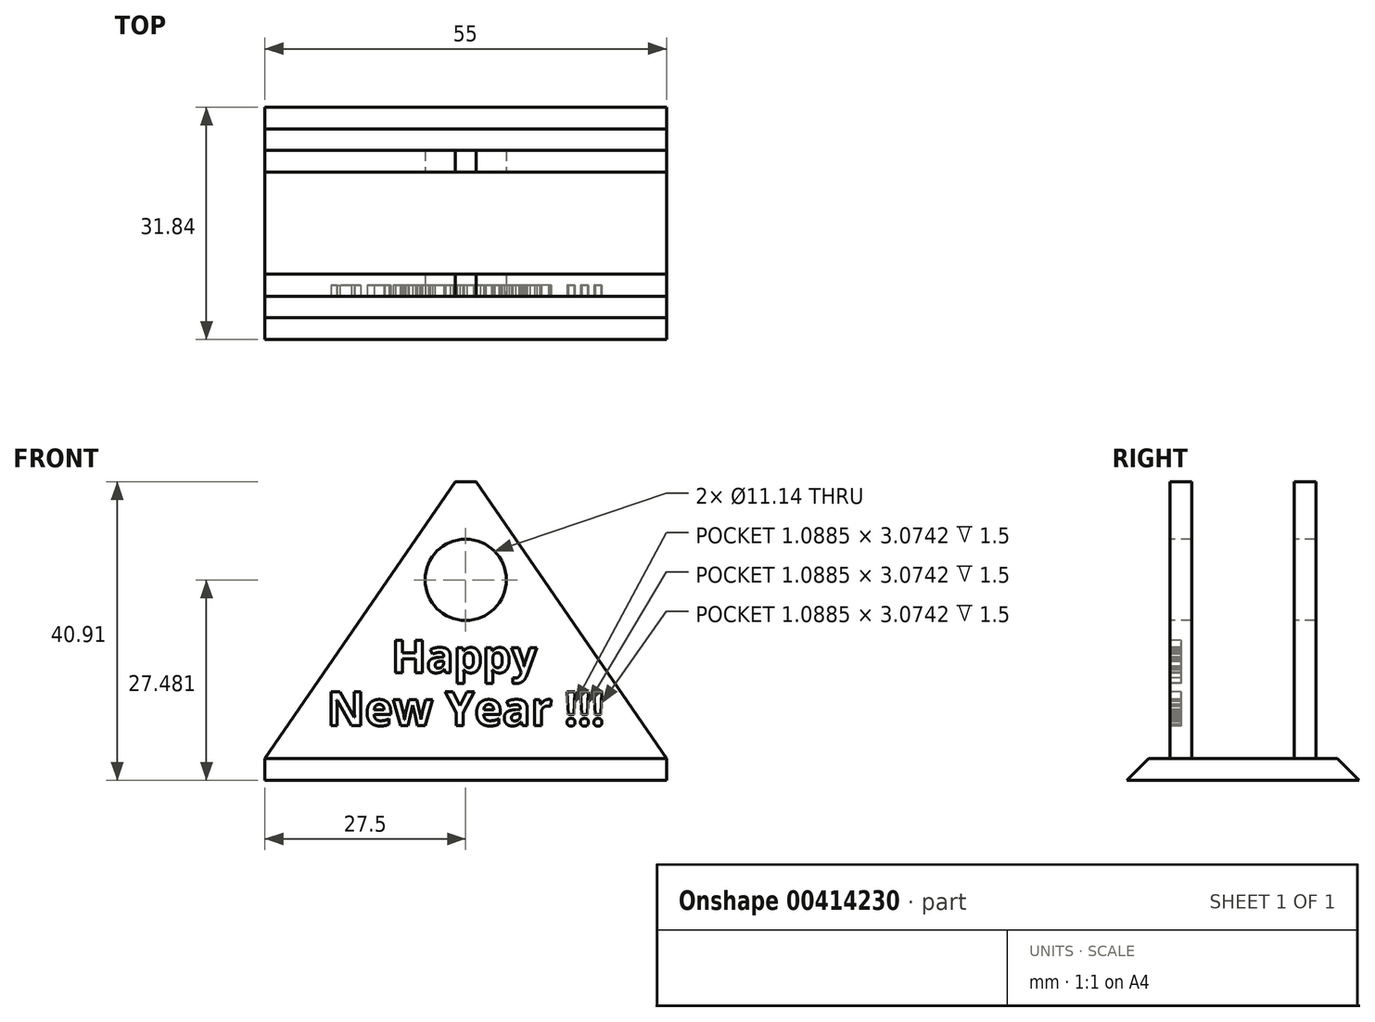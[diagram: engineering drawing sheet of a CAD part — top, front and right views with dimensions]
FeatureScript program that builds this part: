
annotation { "Feature Type Name" : "Feature", "Feature Type Description" : "" }
export const myFeature = defineFeature(function(context is Context, id is Id, definition is map)
    precondition{}
    {
        {
            var Q0;
            Q0=qCreatedBy(makeId("Top.planeOp"),FACE);
            var sketch = newSketch(context, id + "F0", { "sketchPlane" : qUnion([Q0])});
            skLineSegment(sketch, "E0.bottom", {"start": v(27.5, -7) * mm, "end": v(-27.5, -7) * mm});
            skLineSegment(sketch, "E0.top", {"start": v(27.5, 7) * mm, "end": v(-27.5, 7) * mm});
            skLineSegment(sketch, "E0.left", {"start": v(27.5, -7) * mm, "end": v(27.5, 7) * mm});
            skLineSegment(sketch, "E0.right", {"start": v(-27.5, -7) * mm, "end": v(-27.5, 7) * mm});
            skPoint(sketch, "E0.middle", {"position": v(0, 0) * mm});
            skSolve(sketch);
        }
        {
            var Q0;
            Q0=makeQuery(id+"F0.imprint","IMPRINT",FACE,{"disambiguationData":[TD([[makeQuery(id+"F0.imprint","IMPRINT",EDGE,{"derivedFrom":sQuery(id+"F0.wireOp",EDGE,"E0.bottom")}),-1.0]])]});
            extrude(context, id + "F1", {"entities" : qUnion([Q0]), "depth" : 3 * mm});
        }
        {
            var Q0;
            Q0=makeQuery(id+"F1.opExtrude","SWEPT_FACE",FACE,{"disambiguationData":[OSD([sQuery(id+"F0.wireOp",EDGE,"E0.bottom")])]});
            var sketch = newSketch(context, id + "F2", { "sketchPlane" : qUnion([Q0])});
            skLineSegment(sketch, "E1", {"start": v(0, 3) * mm, "end": v(0, 43) * mm, "construction": true});
            skPoint(sketch, "E1.endSnap0", {"position": v(0, 3) * mm});
            skLineSegment(sketch, "E2", {"start": v(0, 43) * mm, "end": v(-27.5, 3) * mm});
            skLineSegment(sketch, "E3", {"start": v(-27.5, 3) * mm, "end": v(-27.5, 0) * mm});
            skLineSegment(sketch, "E4", {"start": v(-27.5, 0) * mm, "end": v(27.5, 0) * mm});
            skLineSegment(sketch, "E5", {"start": v(27.5, 0) * mm, "end": v(27.5, 3) * mm});
            skLineSegment(sketch, "E6", {"start": v(27.5, 3) * mm, "end": v(0, 43) * mm});
            skSolve(sketch);
        }
        {
            var Q0;
            Q0=makeQuery(id+"F2.imprint","IMPRINT",FACE,{"disambiguationData":[TD([[makeQuery(id+"F2.imprint","IMPRINT",EDGE,{"derivedFrom":sQuery(id+"F2.wireOp",EDGE,"E3")}),1.0]])]});
            var Q1;
            Q1=makeQuery(id+"F2.imprint","IMPRINT",FACE,{"disambiguationData":[TD([[makeQuery(id+"F2.imprint","IMPRINT",EDGE,{"derivedFrom":sQuery(id+"F2.wireOp",EDGE,"E2")}),1.0]])]});
            extrude(context, id + "F3", {"entities" : qUnion([Q0, Q1]), "operationType" : NewBodyOperationType.ADD, "depth" : 3 * mm});
        }
        {
            var Q0;
            Q0=makeQuery(id+"F1.opExtrude","SWEPT_FACE",FACE,{"disambiguationData":[OSD([sQuery(id+"F0.wireOp",EDGE,"E0.top")])]});
            var sketch = newSketch(context, id + "F4", { "sketchPlane" : qUnion([Q0])});
            skLineSegment(sketch, "E7", {"start": v(-27.5, 0) * mm, "end": v(-27.5, 3) * mm});
            skLineSegment(sketch, "E8.0", {"start": v(0, 43) * mm, "end": v(27.5, 3) * mm});
            skLineSegment(sketch, "E8.1", {"start": v(-27.5, 3) * mm, "end": v(0, 43) * mm});
            skLineSegment(sketch, "E9", {"start": v(-27.5, 0) * mm, "end": v(27.5, 0) * mm});
            skLineSegment(sketch, "E10", {"start": v(27.5, 0) * mm, "end": v(27.5, 3) * mm});
            skSolve(sketch);
        }
        {
            var Q0;
            Q0=makeQuery(id+"F4.imprint","IMPRINT",FACE,{"disambiguationData":[TD([[makeQuery(id+"F4.imprint","IMPRINT",EDGE,{"derivedFrom":sQuery(id+"F4.wireOp",EDGE,"E8.0")}),-1.0]])]});
            var Q1;
            Q1=makeQuery(id+"F4.imprint","IMPRINT",FACE,{"disambiguationData":[TD([[makeQuery(id+"F4.imprint","IMPRINT",EDGE,{"derivedFrom":sQuery(id+"F4.wireOp",EDGE,"E7")}),1.0]])]});
            extrude(context, id + "F5", {"entities" : qUnion([Q0, Q1]), "operationType" : NewBodyOperationType.ADD, "depth" : 3 * mm});
        }
        {
            var Q0;
            Q0=makeQuery(id+"F5.opExtrude","SWEPT_EDGE",EDGE,{"disambiguationData":[OSD([sQuery(id+"F4.wireOp",EDGE,"E8.0"),sQuery(id+"F4.wireOp",EDGE,"E8.1")])]});
            var Q1;
            Q1=makeQuery(id+"F3.opExtrude","SWEPT_EDGE",EDGE,{"disambiguationData":[OSD([sQuery(id+"F2.wireOp",EDGE,"E2"),sQuery(id+"F2.wireOp",EDGE,"E6")])]});
            chamfer(context, id + "F6", {"entities" : qUnion([Q0, Q1]), "width" : 2.54 * mm, "tangentPropagation" : true});
        }
        {
            var Q0;
            Q0=makeQuery(id+"F3.opExtrude","CAP_FACE",FACE,{"disambiguationData":[OSD([sQuery(id+"F2.wireOp",EDGE,"E2"),sQuery(id+"F2.wireOp",EDGE,"E3"),sQuery(id+"F2.wireOp",EDGE,"E4"),sQuery(id+"F2.wireOp",EDGE,"E5"),sQuery(id+"F2.wireOp",EDGE,"E6")])],"isStart":false});
            var sketch = newSketch(context, id + "F7", { "sketchPlane" : qUnion([Q0])});
            skLineSegment(sketch, "E11.bottom", {"start": v(-27.5, 3) * mm, "end": v(27.5, 3) * mm});
            skLineSegment(sketch, "E11.top", {"start": v(-27.5, 0) * mm, "end": v(27.5, 0) * mm});
            skLineSegment(sketch, "E11.left", {"start": v(-27.5, 3) * mm, "end": v(-27.5, 0) * mm});
            skLineSegment(sketch, "E11.right", {"start": v(27.5, 3) * mm, "end": v(27.5, 0) * mm});
            skSolve(sketch);
        }
        {
            var Q0;
            Q0=makeQuery(id+"F7.imprint","IMPRINT",FACE,{"disambiguationData":[TD([[makeQuery(id+"F7.imprint","IMPRINT",EDGE,{"derivedFrom":sQuery(id+"F7.wireOp",EDGE,"E11.bottom")}),-1.0]])]});
            extrude(context, id + "F8", {"entities" : qUnion([Q0]), "operationType" : NewBodyOperationType.ADD, "depth" : 8 * mm});
        }
        {
            var Q0;
            Q0=makeQuery(id+"F5.opExtrude","CAP_FACE",FACE,{"disambiguationData":[OSD([sQuery(id+"F4.wireOp",EDGE,"E7"),sQuery(id+"F4.wireOp",EDGE,"E8.0"),sQuery(id+"F4.wireOp",EDGE,"E8.1"),sQuery(id+"F4.wireOp",EDGE,"E9"),sQuery(id+"F4.wireOp",EDGE,"E10")])],"isStart":false});
            var sketch = newSketch(context, id + "F9", { "sketchPlane" : qUnion([Q0])});
            skLineSegment(sketch, "E12.bottom", {"start": v(-27.5, 3) * mm, "end": v(27.5, 3) * mm});
            skLineSegment(sketch, "E12.top", {"start": v(-27.5, 0) * mm, "end": v(27.5, 0) * mm});
            skLineSegment(sketch, "E12.left", {"start": v(-27.5, 3) * mm, "end": v(-27.5, 0) * mm});
            skLineSegment(sketch, "E12.right", {"start": v(27.5, 3) * mm, "end": v(27.5, 0) * mm});
            skSolve(sketch);
        }
        {
            var Q0;
            Q0=makeQuery(id+"F9.imprint","IMPRINT",FACE,{"disambiguationData":[TD([[makeQuery(id+"F9.imprint","IMPRINT",EDGE,{"derivedFrom":sQuery(id+"F9.wireOp",EDGE,"E12.bottom")}),-1.0]])]});
            extrude(context, id + "F10", {"entities" : qUnion([Q0]), "operationType" : NewBodyOperationType.ADD, "depth" : 8 * mm});
        }
        {
            var Q0;
            Q0=makeQuery(id+"F10.opExtrude","CAP_EDGE",EDGE,{"disambiguationData":[OSD([sQuery(id+"F9.wireOp",EDGE,"E12.bottom")])],"isStart":false});
            var Q1;
            Q1=makeQuery(id+"F8.opExtrude","CAP_EDGE",EDGE,{"disambiguationData":[OSD([sQuery(id+"F7.wireOp",EDGE,"E11.bottom")])],"isStart":false});
            chamfer(context, id + "F11", {"entities" : qUnion([Q0, Q1]), "width" : 5.08 * mm, "tangentPropagation" : true});
        }
        {
            var Q0;
            Q0=makeQuery(id+"F3.opExtrude","CAP_FACE",FACE,{"disambiguationData":[OSD([sQuery(id+"F2.wireOp",EDGE,"E2"),sQuery(id+"F2.wireOp",EDGE,"E3"),sQuery(id+"F2.wireOp",EDGE,"E4"),sQuery(id+"F2.wireOp",EDGE,"E5"),sQuery(id+"F2.wireOp",EDGE,"E6")])],"isStart":false});
            var sketch = newSketch(context, id + "F12", { "sketchPlane" : qUnion([Q0])});
            skText(sketch, "E13", { "text": "Happy", "fontName": "OpenSans-Bold.ttf"});
            skText(sketch, "E14", { "text": "New Year !!!", "fontName": "OpenSans-Bold.ttf"});
            skLineSegment(sketch, "E15", {"start": v(0, 19.24) * mm, "end": v(0, 22.37) * mm, "construction": true});
            skLineSegment(sketch, "E16", {"start": v(0, 12.15) * mm, "end": v(0, 13.7) * mm, "construction": true});
            const initialGuessF12  = {"E13": [-0.01016, 0.01477, 1, 0, 0.00448], "E14": [-0.01905, 0.00752, 1, 0, 0.00464]};
            skSetInitialGuess(sketch, initialGuessF12);
            skSolve(sketch);
        }
        {
            var Q0;
            Q0 = qSketchRegion(id + "F12", true);
            extrude(context, id + "F13", {"entities" : qUnion([Q0]), "operationType" : NewBodyOperationType.REMOVE, "oppositeDirection" : true, "depth" : 1.5 * mm});
        }
        {
            var Q0;
            {var subQ0=sQuery(id+"F2.wireOp",EDGE,"E6");var subQ1=sQuery(id+"F2.wireOp",EDGE,"E5");var subQ2=sQuery(id+"F2.wireOp",EDGE,"E2");var subQ3=sQuery(id+"F2.wireOp",EDGE,"E3");Q0=makeQuery(id+"F13.boolean.opBoolean","SPLIT",FACE,{"disambiguationData":[TD([makeQuery(id+"F1.opExtrude","SWEPT_FACE",FACE,{"disambiguationData":[OSD([sQuery(id+"F0.wireOp",EDGE,"E0.left")])]})])],"derivedFrom":makeQuery(id+"F3.opExtrude","CAP_FACE",FACE,{"disambiguationData":[OSD([subQ2,subQ3,sQuery(id+"F2.wireOp",EDGE,"E4"),subQ1,subQ0])],"isStart":false})});}
            var sketch = newSketch(context, id + "F14", { "sketchPlane" : qUnion([Q0])});
            skCircle(sketch, "E17", {"center": v(0, 27.48) * mm, "radius": 5.57 * mm});
            skSolve(sketch);
        }
        {
            var Q0;
            Q0=makeQuery(id+"F14.imprint","IMPRINT",FACE,{"disambiguationData":[TD([[makeQuery(id+"F14.imprint","IMPRINT",EDGE,{"derivedFrom":sQuery(id+"F14.wireOp",EDGE,"E17")}),1.0]])]});
            extrude(context, id + "F15", {"entities" : qUnion([Q0]), "operationType" : NewBodyOperationType.REMOVE, "endBound" : BoundingType.THROUGH_ALL, "oppositeDirection" : true, "depth" : 25.4 * mm});
        }
    });
